# Revit family: E-930_RFA
name_source: partatom
category: Aparatos sanitarios
units: mm (PartAtom-declared; Revit-internal decimal feet)

## family parameters
Compartido = Sí
Corte con vacíos al cargar = No
Cota de conector redondo = Diámetro de uso
Número OmniClass = 23.45.55.14
Punto de cálculo de habitación = Sí
Se basa en plano de trabajo = Sí
Siempre vertical = Sí
Tipo de pieza = Normal
Título OmniClass = Single Faucets

## types (1)
- E-930
    Accesorios = Contra de push, Inserto para lavabo sin rebosadero, Herramienta para sujeción, Llave de mantenimiento, Llave allen 5/64"
    Características del Producto = Monomando para lavabo con contra de push
    Comentarios de tipo = Monomando de lavabo. Incluye contra de push. Incluye inserto para usarse con lavabos sin rebosadero. Compatible con lavabos de sobreponer (1 orificio), sobrecubierta o bajocubierta.
    Cuerpo de Latón = Brass
    Descripción = Monomando para lavabo con contra de push
    Elevación por defecto = 1"
    Fabricante = HELVEX S.A. de C.V.
    Garantía = El producto HELVEX está garantizado como libre de defectos en materiales y procesos de fabricación. El producto HELVEX está garantizado, en lo que se refiere a los acabados; por un periodo de 10 años en los acabados cromo y duravex, y por 2 años en acabados diferentes al cromo, a partir de la fecha de compra indicada en la factura
    Imagen de tipo = E-930.png
    Instalación = Conexión ½ - 14 NPSM
    Modelo = E-930
    Operación = Levante el maneral para abrir el flujo y gire a la derecha para mas fría o a la izquierda para más caliente
    Presión Máxima de Trabajo = 85.3 psi
    Presión Mínima de Trabajo = 3.6 psi
    Total Depth = 9"
    Total Height = 9"
    Total Width = 2"
    URL = https://helvex.com.mx

## geometry (parser evidence)
native form markers: Sweep x3
no freeform markers — native parametric forms only
